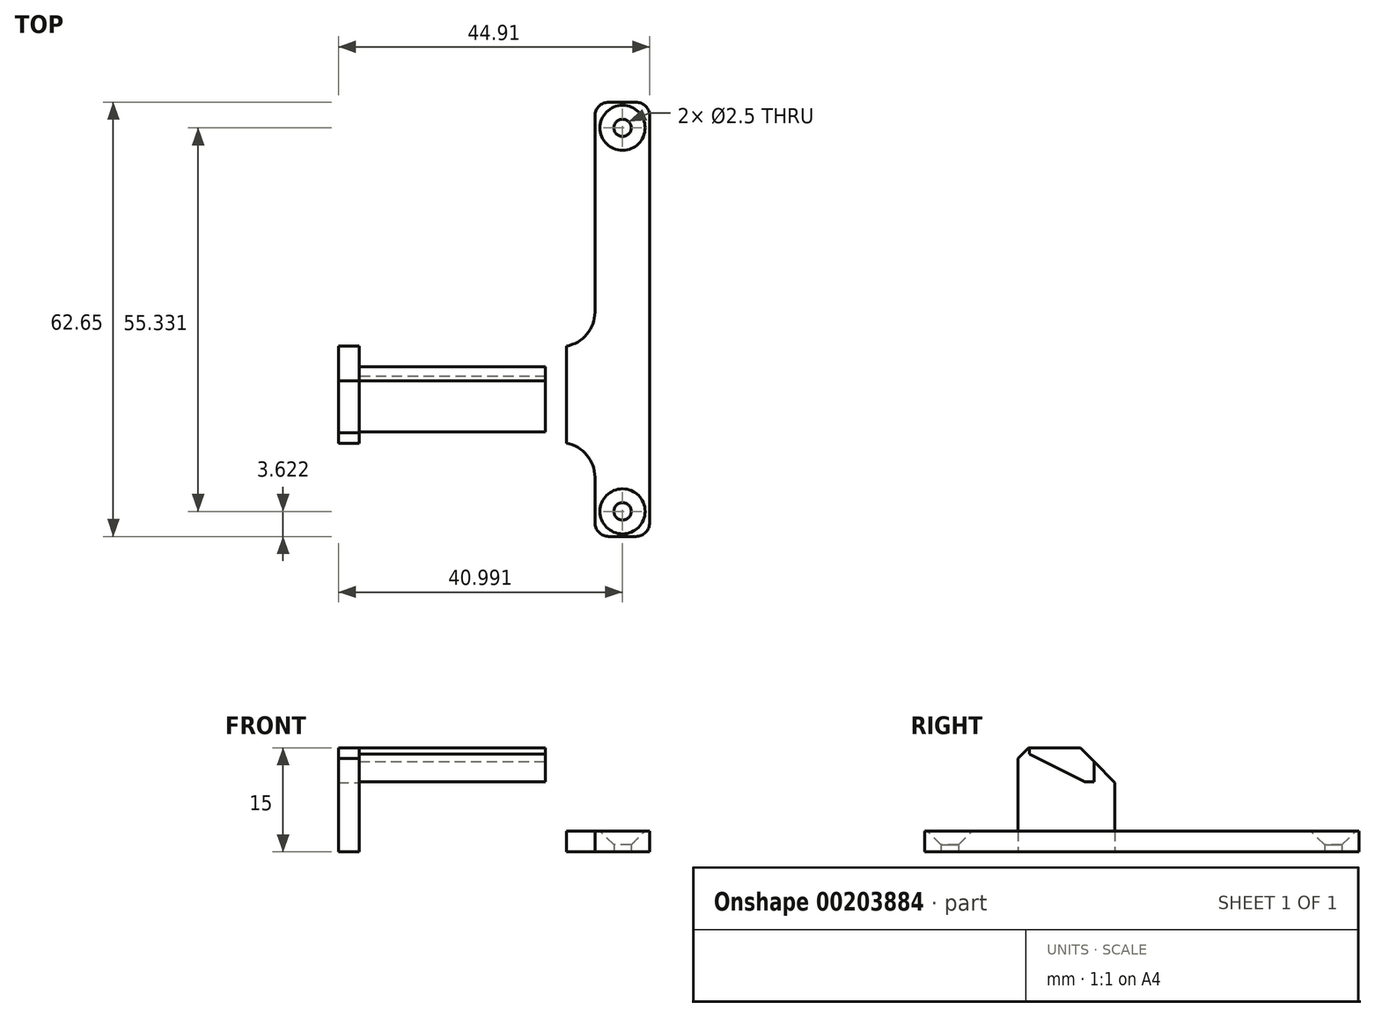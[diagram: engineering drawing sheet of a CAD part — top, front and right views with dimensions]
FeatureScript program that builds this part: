
annotation { "Feature Type Name" : "Feature", "Feature Type Description" : "" }
export const myFeature = defineFeature(function(context is Context, id is Id, definition is map)
    precondition{}
    {
        {
            var Q0;
            Q0=qCreatedBy(makeId("Top.planeOp"),FACE);
            var sketch = newSketch(context, id + "F0", { "sketchPlane" : qUnion([Q0])});
            skLineSegment(sketch, "E0.bottom", {"start": v(-36.58, 47.75) * mm, "end": v(22.42, 47.75) * mm});
            skLineSegment(sketch, "E0.top", {"start": v(-36.58, -16.75) * mm, "end": v(22.42, -16.75) * mm});
            skLineSegment(sketch, "E0.left", {"start": v(-36.58, 47.75) * mm, "end": v(-36.58, -16.75) * mm});
            skLineSegment(sketch, "E0.right", {"start": v(22.42, 47.75) * mm, "end": v(22.42, -16.75) * mm});
            skCircle(sketch, "E1", {"center": v(-31.8, 43) * mm, "radius": 2.5 * mm});
            skCircle(sketch, "E2", {"center": v(-31.8, 43) * mm, "radius": 1.25 * mm});
            skCircle(sketch, "E3", {"center": v(17.5, 43.01) * mm, "radius": 2.5 * mm});
            skCircle(sketch, "E4", {"center": v(17.5, 43.01) * mm, "radius": 1.25 * mm});
            skLineSegment(sketch, "E5.bottom", {"start": v(-20.3, -2.46) * mm, "end": v(6.08, -2.46) * mm});
            skLineSegment(sketch, "E5.top", {"start": v(-20.3, 7.9) * mm, "end": v(6.08, 7.9) * mm});
            skLineSegment(sketch, "E5.left", {"start": v(-20.3, -2.46) * mm, "end": v(-20.3, 7.9) * mm});
            skLineSegment(sketch, "E5.right", {"start": v(6.08, -2.46) * mm, "end": v(6.08, 7.9) * mm});
            skLineSegment(sketch, "E6.bottom", {"start": v(13.5, 46.71) * mm, "end": v(21.41, 46.71) * mm});
            skLineSegment(sketch, "E6.top", {"start": v(13.5, -2.53) * mm, "end": v(21.41, -2.53) * mm});
            skLineSegment(sketch, "E6.left", {"start": v(13.5, 46.71) * mm, "end": v(13.5, -2.53) * mm});
            skLineSegment(sketch, "E6.right", {"start": v(21.41, 46.71) * mm, "end": v(21.41, -2.53) * mm});
            skLineSegment(sketch, "E7.bottom", {"start": v(13.5, 11.52) * mm, "end": v(-20.5, 11.52) * mm});
            skLineSegment(sketch, "E7.top", {"start": v(13.5, 8.52) * mm, "end": v(-20.5, 8.52) * mm});
            skLineSegment(sketch, "E7.left", {"start": v(13.5, 11.52) * mm, "end": v(13.5, 8.52) * mm});
            skLineSegment(sketch, "E7.right", {"start": v(-20.5, 11.52) * mm, "end": v(-20.5, 8.52) * mm});
            skLineSegment(sketch, "E8.bottom", {"start": v(-20.5, 11.52) * mm, "end": v(-23.5, 11.52) * mm});
            skLineSegment(sketch, "E8.top", {"start": v(-20.5, -2.48) * mm, "end": v(-23.5, -2.48) * mm});
            skLineSegment(sketch, "E8.left", {"start": v(-20.5, 11.52) * mm, "end": v(-20.5, -2.48) * mm});
            skLineSegment(sketch, "E8.right", {"start": v(-23.5, 11.52) * mm, "end": v(-23.5, -2.48) * mm});
            skLineSegment(sketch, "E9.bottom", {"start": v(9.38, 8.52) * mm, "end": v(6.38, 8.52) * mm});
            skLineSegment(sketch, "E9.top", {"start": v(9.38, -2.48) * mm, "end": v(6.38, -2.48) * mm});
            skLineSegment(sketch, "E9.left", {"start": v(9.38, 8.52) * mm, "end": v(9.38, -2.48) * mm});
            skLineSegment(sketch, "E9.right", {"start": v(6.38, 8.52) * mm, "end": v(6.38, -2.48) * mm});
            skLineSegment(sketch, "E10", {"start": v(13.5, -2.53) * mm, "end": v(9.38, -2.48) * mm});
            skLineSegment(sketch, "E11", {"start": v(9.38, 8.52) * mm, "end": v(9.38, 11.52) * mm});
            skLineSegment(sketch, "E12", {"start": v(-20.5, -0.85) * mm, "end": v(6.38, -0.85) * mm});
            skCircle(sketch, "E13", {"center": v(17.5, -12.32) * mm, "radius": 2.5 * mm});
            skCircle(sketch, "E14", {"center": v(17.5, -12.32) * mm, "radius": 1.25 * mm});
            skLineSegment(sketch, "E15.bottom", {"start": v(13.5, -2.53) * mm, "end": v(19.82, -2.54) * mm});
            skLineSegment(sketch, "E16.bottom", {"start": v(13.5, -2.53) * mm, "end": v(21.4, -2.53) * mm});
            skLineSegment(sketch, "E16.top", {"start": v(13.5, -15.94) * mm, "end": v(21.4, -15.94) * mm});
            skLineSegment(sketch, "E16.left", {"start": v(13.5, -2.53) * mm, "end": v(13.5, -15.94) * mm});
            skLineSegment(sketch, "E16.right", {"start": v(21.4, -2.53) * mm, "end": v(21.4, -15.94) * mm});
            skSolve(sketch);
        }
        {
            var Q0;
            {var subQ3=sQuery(id+"F0.wireOp",EDGE,"E8.bottom");Q0=makeQuery(id+"F0.imprint","IMPRINT",FACE,{"disambiguationData":[TD([[makeQuery(id+"F0.imprint","IMPRINT",EDGE,{"derivedFrom":subQ3}),1.0]])]});}
            var Q1;
            {var subQ5=sQuery(id+"F0.wireOp",EDGE,"E7.bottom");Q1=makeQuery(id+"F0.imprint","IMPRINT",FACE,{"disambiguationData":[TD([[makeQuery(id+"F0.imprint","IMPRINT",EDGE,{"derivedFrom":subQ5}),1.0]])]});}
            var Q2;
            Q2=makeQuery(id+"F0.imprint","IMPRINT",FACE,{"disambiguationData":[TD([[makeQuery(id+"F0.imprint","IMPRINT",EDGE,{"derivedFrom":sQuery(id+"F0.wireOp",EDGE,"E9.bottom")}),1.0]])]});
            var Q3;
            {var subQ4=sQuery(id+"F0.wireOp",EDGE,"E9.left");Q3=makeQuery(id+"F0.imprint","IMPRINT",FACE,{"disambiguationData":[TD([[makeQuery(id+"F0.imprint","IMPRINT",EDGE,{"derivedFrom":subQ4}),1.0]])]});}
            var Q4;
            {var subQ1=sQuery(id+"F0.wireOp",EDGE,"E6.top");Q4=makeQuery(id+"F0.imprint","IMPRINT",FACE,{"disambiguationData":[TD([[makeQuery(id+"F0.imprint","IMPRINT",EDGE,{"derivedFrom":subQ1}),1.0]])]});}
            var Q5;
            Q5=makeQuery(id+"F0.imprint","IMPRINT",FACE,{"disambiguationData":[TD([[makeQuery(id+"F0.imprint","IMPRINT",EDGE,{"derivedFrom":sQuery(id+"F0.wireOp",EDGE,"E4")}),-1.0]])]});
            var Q6;
            {var subQ0=sQuery(id+"F0.wireOp",EDGE,"E9.bottom");Q6=makeQuery(id+"F0.imprint","IMPRINT",FACE,{"disambiguationData":[TD([[makeQuery(id+"F0.imprint","IMPRINT",EDGE,{"derivedFrom":subQ0}),-1.0]])]});}
            extrude(context, id + "F1", {"entities" : qUnion([Q0, Q1, Q2, Q3, Q4, Q5, Q6]), "depth" : 3 * mm, "offsetDistance" : 25 * mm});
        }
        {
            var Q0;
            {var subQ3=sQuery(id+"F0.wireOp",EDGE,"E8.bottom");Q0=makeQuery(id+"F0.imprint","IMPRINT",FACE,{"disambiguationData":[TD([[makeQuery(id+"F0.imprint","IMPRINT",EDGE,{"derivedFrom":subQ3}),1.0]])]});}
            var Q1;
            {var subQ0=sQuery(id+"F0.wireOp",EDGE,"E9.bottom");Q1=makeQuery(id+"F0.imprint","IMPRINT",FACE,{"disambiguationData":[TD([[makeQuery(id+"F0.imprint","IMPRINT",EDGE,{"derivedFrom":subQ0}),-1.0]])]});}
            var Q2;
            Q2=makeQuery(id+"F0.imprint","IMPRINT",FACE,{"disambiguationData":[TD([[makeQuery(id+"F0.imprint","IMPRINT",EDGE,{"derivedFrom":sQuery(id+"F0.wireOp",EDGE,"E9.bottom")}),1.0]])]});
            extrude(context, id + "F2", {"entities" : qUnion([Q0, Q1, Q2]), "operationType" : NewBodyOperationType.ADD, "depth" : 15 * mm, "offsetDistance" : 25 * mm});
        }
        {
            var Q0;
            {var subQ0=sQuery(id+"F0.wireOp",EDGE,"E5.top");Q0=makeQuery(id+"F0.imprint","IMPRINT",FACE,{"disambiguationData":[TD([[makeQuery(id+"F0.imprint","IMPRINT",EDGE,{"derivedFrom":subQ0}),-1.0]])]});}
            var Q1;
            {var subQ1=sQuery(id+"F0.wireOp",EDGE,"E5.top");Q1=makeQuery(id+"F0.imprint","IMPRINT",FACE,{"disambiguationData":[TD([[makeQuery(id+"F0.imprint","IMPRINT",EDGE,{"derivedFrom":subQ1}),1.0]])]});}
            extrude(context, id + "F3", {"entities" : qUnion([Q0, Q1]), "depth" : 15 * mm, "offsetDistance" : 25 * mm, "hasSecondDirection" : true, "secondDirectionOppositeDirection" : false, "secondDirectionDepth" : 10.1 * mm});
        }
        {
            var Q0;
            Q0=makeQuery(id+"F2.opExtrude","CAP_EDGE",EDGE,{"disambiguationData":[OSD([sQuery(id+"F0.wireOp",EDGE,"E8.top")])],"isStart":false});
            var Q1;
            Q1=makeQuery(id+"F2.opExtrude","CAP_EDGE",EDGE,{"disambiguationData":[OSD([sQuery(id+"F0.wireOp",EDGE,"E9.top")])],"isStart":false});
            chamfer(context, id + "F4", {"entities" : qUnion([Q0, Q1]), "width" : 1.5 * mm, "tangentPropagation" : true});
        }
        {
            var Q0;
            Q0=makeQuery(id+"F1.opExtrude","CAP_EDGE",EDGE,{"disambiguationData":[OSD([sQuery(id+"F0.wireOp",EDGE,"E4")])],"isStart":false});
            chamfer(context, id + "F5", {"entities" : qUnion([Q0]), "width" : 2 * mm, "tangentPropagation" : true});
        }
        {
            var Q0;
            {var subQ1=sQuery(id+"F0.wireOp",EDGE,"E15.bottom");Q0=makeQuery(id+"F0.imprint","IMPRINT",FACE,{"disambiguationData":[TD([[makeQuery(id+"F0.imprint","IMPRINT",EDGE,{"derivedFrom":subQ1}),-1.0]])]});}
            var Q1;
            Q1=makeQuery(id+"F0.imprint","IMPRINT",FACE,{"disambiguationData":[TD([[makeQuery(id+"F0.imprint","IMPRINT",EDGE,{"derivedFrom":sQuery(id+"F0.wireOp",EDGE,"E14")}),-1.0]])]});
            var Q2;
            Q2=makeQuery(id+"F0.imprint","IMPRINT",FACE,{"disambiguationData":[TD([[makeQuery(id+"F0.imprint","IMPRINT",EDGE,{"derivedFrom":sQuery(id+"F0.wireOp",EDGE,"E13")}),-1.0]])]});
            extrude(context, id + "F6", {"entities" : qUnion([Q0, Q1, Q2]), "operationType" : NewBodyOperationType.ADD, "depth" : 3 * mm, "offsetDistance" : 25 * mm});
        }
        {
            var Q0;
            Q0=makeQuery(id+"F6.opExtrude","CAP_EDGE",EDGE,{"disambiguationData":[OSD([sQuery(id+"F0.wireOp",EDGE,"E14")])],"isStart":false});
            chamfer(context, id + "F7", {"entities" : qUnion([Q0]), "width" : 2 * mm, "tangentPropagation" : true});
        }
        {
            var Q0;
            Q0=makeQuery(id+"F6.opExtrude","SWEPT_EDGE",EDGE,{"disambiguationData":[OSD([sQuery(id+"F0.wireOp",EDGE,"E16.top"),sQuery(id+"F0.wireOp",EDGE,"E16.right")])]});
            var Q1;
            Q1=makeQuery(id+"F6.opExtrude","SWEPT_EDGE",EDGE,{"disambiguationData":[OSD([sQuery(id+"F0.wireOp",EDGE,"E16.top"),sQuery(id+"F0.wireOp",EDGE,"E16.left")])]});
            var Q2;
            Q2=makeQuery(id+"F1.opExtrude","SWEPT_EDGE",EDGE,{"disambiguationData":[OSD([sQuery(id+"F0.wireOp",EDGE,"E6.bottom"),sQuery(id+"F0.wireOp",EDGE,"E6.right")])]});
            var Q3;
            Q3=makeQuery(id+"F1.opExtrude","SWEPT_EDGE",EDGE,{"disambiguationData":[OSD([sQuery(id+"F0.wireOp",EDGE,"E6.bottom"),sQuery(id+"F0.wireOp",EDGE,"E6.left")])]});
            fillet(context, id + "F8", {"entities" : qUnion([Q0, Q1, Q2, Q3]), "radius" : 2 * mm, "tangentPropagation" : true, "allowEdgeOverflow" : false});
        }
        {
            var Q0;
            Q0=makeQuery(id+"F1.opExtrude","SWEPT_EDGE",EDGE,{"disambiguationData":[OSD([sQuery(id+"F0.wireOp",EDGE,"E6.left"),sQuery(id+"F0.wireOp",EDGE,"E7.bottom"),sQuery(id+"F0.wireOp",EDGE,"E7.left")])]});
            var Q1;
            {var subQ0=sQuery(id+"F0.wireOp",EDGE,"E16.left");var subQ1=sQuery(id+"F0.wireOp",EDGE,"E16.bottom");var subQ2=sQuery(id+"F0.wireOp",EDGE,"E15.bottom");var subQ3=sQuery(id+"F0.wireOp",EDGE,"E10");var subQ4=sQuery(id+"F0.wireOp",EDGE,"E6.left");Q1=makeQuery(id+"F6.boolean.opBoolean","MERGE",EDGE,{"derivedFrom":[makeQuery(id+"F1.opExtrude","SWEPT_EDGE",EDGE,{"disambiguationData":[OSD([subQ4,subQ3,subQ2,subQ1,subQ0])]}),makeQuery(id+"F6.opExtrude","SWEPT_EDGE",EDGE,{"disambiguationData":[OSD([subQ4,subQ3,subQ2,subQ1,subQ0])]})]});}
            fillet(context, id + "F9", {"entities" : qUnion([Q0, Q1]), "radius" : 5 * mm, "tangentPropagation" : true, "allowEdgeOverflow" : false});
        }
        {
            var Q0;
            Q0=makeQuery(id+"F2.opExtrude","CAP_EDGE",EDGE,{"disambiguationData":[OSD([sQuery(id+"F0.wireOp",EDGE,"E7.bottom"),sQuery(id+"F0.wireOp",EDGE,"E8.bottom")])],"isStart":false});
            chamfer(context, id + "F10", {"entities" : qUnion([Q0]), "width" : 5 * mm, "tangentPropagation" : true});
        }
        {
            var Q0;
            Q0=makeQuery(id+"F3.opExtrude","CAP_EDGE",EDGE,{"disambiguationData":[OSD([sQuery(id+"F0.wireOp",EDGE,"E7.top")])],"isStart":false});
            chamfer(context, id + "F11", {"entities" : qUnion([Q0]), "width" : 2 * mm, "tangentPropagation" : true});
        }
        {
            var Q0;
            Q0=makeQuery(id+"F3.opExtrude","CAP_EDGE",EDGE,{"disambiguationData":[OSD([sQuery(id+"F0.wireOp",EDGE,"E12")])],"isStart":true});
            chamfer(context, id + "F12", {"entities" : qUnion([Q0]), "chamferType" : ChamferType.TWO_OFFSETS, "width1" : 4 * mm, "oppositeDirection" : false, "width2" : 8 * mm, "tangentPropagation" : true});
        }
    });
